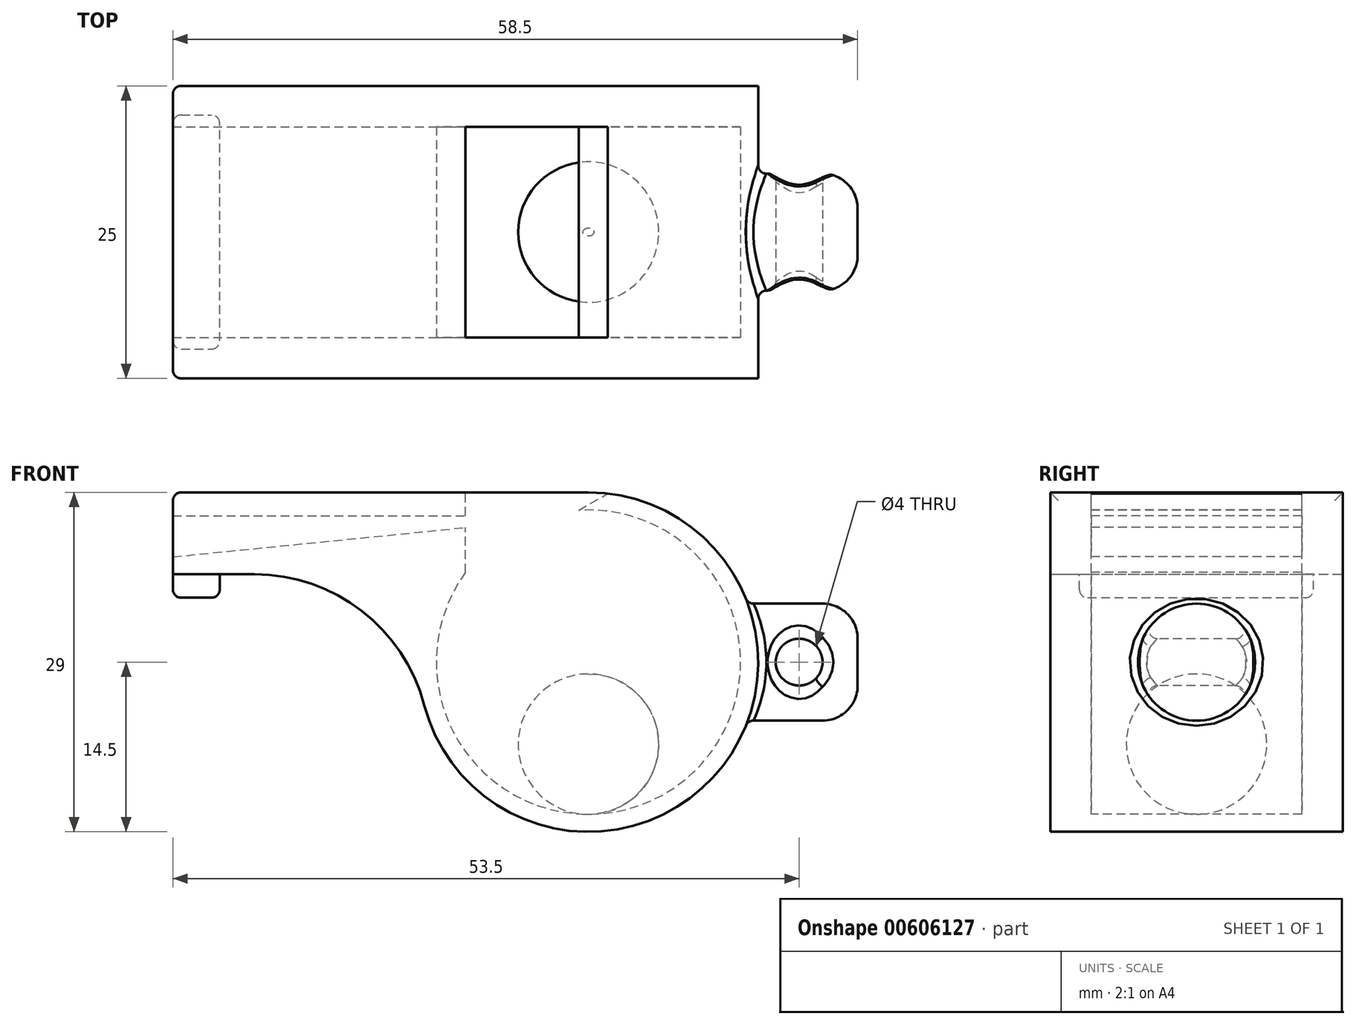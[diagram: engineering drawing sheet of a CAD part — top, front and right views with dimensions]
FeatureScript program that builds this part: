
annotation { "Feature Type Name" : "Feature", "Feature Type Description" : "" }
export const myFeature = defineFeature(function(context is Context, id is Id, definition is map)
    precondition{}
    {
        {
            var Q0;
            Q0=qCreatedBy(makeId("Front.planeOp"),FACE);
            var sketch = newSketch(context, id + "F0", { "sketchPlane" : qUnion([Q0])});
            skArc(sketch, "E0", {"start": v(-12.4, 7.5) * mm, "mid": v(7.12, -12.63) * mm, "end": v(0, 14.5) * mm});
            skLineSegment(sketch, "E1.bottom", {"start": v(0, 14.5) * mm, "end": v(-35.5, 14.5) * mm});
            skLineSegment(sketch, "E1.top", {"start": v(-12.4, 7.5) * mm, "end": v(-35.5, 7.5) * mm});
            skLineSegment(sketch, "E1.right", {"start": v(-35.5, 14.5) * mm, "end": v(-35.5, 7.5) * mm});
            skSolve(sketch);
        }
        {
            var Q0;
            Q0 = qSketchRegion(id + "F0", true);
            extrude(context, id + "F1", {"entities" : qUnion([Q0]), "endBound" : BoundingType.SYMMETRIC, "depth" : 25 * mm, "offsetDistance" : 25 * mm});
        }
        {
            var Q0;
            Q0=qCreatedBy(makeId("Front.planeOp"),FACE);
            var sketch = newSketch(context, id + "F2", { "sketchPlane" : qUnion([Q0])});
            skArc(sketch, "E2", {"start": v(-10.5, 7.66) * mm, "mid": v(5.89, -11.59) * mm, "end": v(0, 13) * mm});
            skLineSegment(sketch, "E3", {"start": v(-10.5, 7.66) * mm, "end": v(-10.5, 11.5) * mm});
            skLineSegment(sketch, "E4", {"start": v(-35.5, 12.5) * mm, "end": v(-10.5, 12.5) * mm});
            skLineSegment(sketch, "E5", {"start": v(-10.5, 12.5) * mm, "end": v(-10.5, 14.5) * mm});
            skLineSegment(sketch, "E6", {"start": v(-10.5, 14.5) * mm, "end": v(0, 14.5) * mm});
            skArc(sketch, "E7", {"start": v(-10.5, 7.66) * mm, "mid": v(6.26, -11.4) * mm, "end": v(-0.83, 12.97) * mm});
            skLineSegment(sketch, "E8", {"start": v(-35.5, 12.5) * mm, "end": v(-35.5, 9) * mm});
            skLineSegment(sketch, "E9", {"start": v(-35.5, 9) * mm, "end": v(-10.5, 11.5) * mm});
            skLineSegment(sketch, "E10", {"start": v(0, 13) * mm, "end": v(-0.83, 12.97) * mm});
            skLineSegment(sketch, "E11", {"start": v(0, 14.5) * mm, "end": v(1.81, 14.5) * mm});
            skLineSegment(sketch, "E12", {"start": v(-0.83, 12.97) * mm, "end": v(1.81, 14.5) * mm});
            skSolve(sketch);
        }
        {
            var Q0;
            Q0 = qSketchRegion(id + "F2", true);
            extrude(context, id + "F3", {"entities" : qUnion([Q0]), "operationType" : NewBodyOperationType.REMOVE, "endBound" : BoundingType.SYMMETRIC, "oppositeDirection" : true, "depth" : 18 * mm, "offsetDistance" : 25 * mm});
        }
        {
            var Q0;
            Q0=qCreatedBy(makeId("Front.planeOp"),FACE);
            var sketch = newSketch(context, id + "F4", { "sketchPlane" : qUnion([Q0])});
            skLineSegment(sketch, "E13", {"start": v(0, 0) * mm, "end": v(23, 0) * mm});
            skLineSegment(sketch, "E14.bottom", {"start": v(23, 0) * mm, "end": v(13, 0) * mm});
            skLineSegment(sketch, "E14.top", {"start": v(23, 5) * mm, "end": v(13, 5) * mm});
            skLineSegment(sketch, "E14.left", {"start": v(23, 0) * mm, "end": v(23, 5) * mm});
            skLineSegment(sketch, "E14.right", {"start": v(13, 0) * mm, "end": v(13, 5) * mm});
            skSolve(sketch);
        }
        {
            var Q0;
            Q0 = qSketchRegion(id + "F4", true);
            var Q1;
            Q1=sQuery(id+"F4.wireOp",EDGE,"E14.bottom");
            revolve(context, id + "F5", {"operationType" : NewBodyOperationType.ADD, "entities" : qUnion([Q0]), "axis" : qUnion([Q1]), "revolveType" : RevolveType.FULL});
        }
        {
            var Q0;
            Q0=makeQuery(id+"F5.opRevolve","SWEPT_EDGE",EDGE,{"disambiguationData":[OSD([sQuery(id+"F4.wireOp",EDGE,"E14.top"),sQuery(id+"F4.wireOp",EDGE,"E14.left")])]});
            fillet(context, id + "F6", {"entities" : qUnion([Q0]), "radius" : 3 * mm, "tangentPropagation" : true, "allowEdgeOverflow" : false});
        }
        {
            var Q0;
            Q0=qCreatedBy(makeId("Front.planeOp"),FACE);
            var sketch = newSketch(context, id + "F7", { "sketchPlane" : qUnion([Q0])});
            skCircle(sketch, "E15", {"center": v(18, 0) * mm, "radius": 2 * mm});
            skSolve(sketch);
        }
        {
            var Q0;
            Q0 = qSketchRegion(id + "F7", true);
            extrude(context, id + "F8", {"entities" : qUnion([Q0]), "operationType" : NewBodyOperationType.REMOVE, "endBound" : BoundingType.SYMMETRIC, "oppositeDirection" : true, "depth" : 10 * mm, "offsetDistance" : 25 * mm});
        }
        {
            var Q0;
            Q0=makeQuery(id+"F1.opExtrude","SWEPT_FACE",FACE,{"disambiguationData":[OSD([sQuery(id+"F0.wireOp",EDGE,"E1.top")])]});
            var sketch = newSketch(context, id + "F9", { "sketchPlane" : qUnion([Q0])});
            skLineSegment(sketch, "E16.bottom", {"start": v(-35.5, 10) * mm, "end": v(-31.5, 10) * mm});
            skLineSegment(sketch, "E16.top", {"start": v(-35.5, -10) * mm, "end": v(-31.5, -10) * mm});
            skLineSegment(sketch, "E16.left", {"start": v(-35.5, 10) * mm, "end": v(-35.5, -10) * mm});
            skLineSegment(sketch, "E16.right", {"start": v(-31.5, 10) * mm, "end": v(-31.5, -10) * mm});
            skSolve(sketch);
        }
        {
            var Q0;
            Q0 = qSketchRegion(id + "F9", true);
            extrude(context, id + "F10", {"entities" : qUnion([Q0]), "operationType" : NewBodyOperationType.ADD, "depth" : 2 * mm, "offsetDistance" : 25 * mm});
        }
        {
            var Q0;
            Q0=makeQuery(id+"F10.opExtrude","SWEPT_EDGE",EDGE,{"disambiguationData":[OSD([sQuery(id+"F0.wireOp",EDGE,"E1.top"),sQuery(id+"F0.wireOp",EDGE,"E1.right"),sQuery(id+"F9.wireOp",EDGE,"E16.bottom"),sQuery(id+"F9.wireOp",EDGE,"E16.left")])]});
            var Q1;
            Q1=makeQuery(id+"F10.opExtrude","CAP_EDGE",EDGE,{"disambiguationData":[OSD([sQuery(id+"F9.wireOp",EDGE,"E16.bottom")])],"isStart":false});
            var Q2;
            Q2=makeQuery(id+"F10.opExtrude","SWEPT_EDGE",EDGE,{"disambiguationData":[OSD([sQuery(id+"F9.wireOp",EDGE,"E16.bottom"),sQuery(id+"F9.wireOp",EDGE,"E16.right")])]});
            var Q3;
            Q3=makeQuery(id+"F10.opExtrude","CAP_EDGE",EDGE,{"disambiguationData":[OSD([sQuery(id+"F9.wireOp",EDGE,"E16.right")])],"isStart":false});
            var Q4;
            Q4=makeQuery(id+"F10.opExtrude","CAP_EDGE",EDGE,{"disambiguationData":[OSD([sQuery(id+"F9.wireOp",EDGE,"E16.top")])],"isStart":false});
            var Q5;
            Q5=makeQuery(id+"F10.opExtrude","CAP_EDGE",EDGE,{"disambiguationData":[OSD([sQuery(id+"F9.wireOp",EDGE,"E16.left")])],"isStart":false});
            var Q6;
            Q6=makeQuery(id+"F10.opExtrude","SWEPT_EDGE",EDGE,{"disambiguationData":[OSD([sQuery(id+"F9.wireOp",EDGE,"E16.top"),sQuery(id+"F9.wireOp",EDGE,"E16.right")])]});
            var Q7;
            Q7=makeQuery(id+"F10.opExtrude","SWEPT_EDGE",EDGE,{"disambiguationData":[OSD([sQuery(id+"F0.wireOp",EDGE,"E1.top"),sQuery(id+"F0.wireOp",EDGE,"E1.right"),sQuery(id+"F9.wireOp",EDGE,"E16.top"),sQuery(id+"F9.wireOp",EDGE,"E16.left")])]});
            var Q8;
            Q8=makeQuery(id+"F1.opExtrude","CAP_EDGE",EDGE,{"disambiguationData":[OSD([sQuery(id+"F0.wireOp",EDGE,"E1.right")])],"isStart":false});
            var Q9;
            Q9=makeQuery(id+"F1.opExtrude","SWEPT_EDGE",EDGE,{"disambiguationData":[OSD([sQuery(id+"F0.wireOp",EDGE,"E1.bottom"),sQuery(id+"F0.wireOp",EDGE,"E1.right")])]});
            var Q10;
            Q10=makeQuery(id+"F1.opExtrude","CAP_EDGE",EDGE,{"disambiguationData":[OSD([sQuery(id+"F0.wireOp",EDGE,"E1.right")])],"isStart":true});
            var Q11;
            {var subQ0=sQuery(id+"F4.wireOp",EDGE,"E14.left");Q11=makeQuery(id+"F6.opFillet","BLEND_EDGE",EDGE,{"blendedFrom":[makeQuery(id+"F5.opRevolve","SWEPT_EDGE",EDGE,{"disambiguationData":[OSD([sQuery(id+"F4.wireOp",EDGE,"E14.top"),subQ0])]}),makeQuery(id+"F5.opRevolve","SWEPT_FACE",FACE,{"disambiguationData":[OSD([subQ0])]})],"blendedInto":[makeQuery(id+"F5.opRevolve","SWEPT_FACE",FACE,{"disambiguationData":[OSD([subQ0])]})]});}
            var Q12;
            Q12=makeQuery(id+"F6.opFillet","BLEND_FACE",FACE,{"disambiguationData":[OSD([sQuery(id+"F4.wireOp",EDGE,"E14.top"),sQuery(id+"F4.wireOp",EDGE,"E14.left")])]});
            var Q13;
            Q13=makeQuery(id+"F5.boolean.opBoolean","INTERSECT",EDGE,{"derivedFrom":[makeQuery(id+"F1.opExtrude","SWEPT_FACE",FACE,{"disambiguationData":[OSD([sQuery(id+"F0.wireOp",EDGE,"E0")])]}),makeQuery(id+"F5.opRevolve","SWEPT_FACE",FACE,{"disambiguationData":[OSD([sQuery(id+"F4.wireOp",EDGE,"E14.top")])]})]});
            var Q14;
            Q14=makeQuery(id+"F5.opRevolve","SWEPT_FACE",FACE,{"disambiguationData":[OSD([sQuery(id+"F4.wireOp",EDGE,"E14.left")])]});
            var Q15;
            Q15=makeQuery(id+"F8.boolean.opBoolean","INTERSECT",EDGE,{"disambiguationData":[OD(0.0)],"derivedFrom":[makeQuery(id+"F5.opRevolve","SWEPT_FACE",FACE,{"disambiguationData":[OSD([sQuery(id+"F4.wireOp",EDGE,"E14.top")])]}),makeQuery(id+"F8.opExtrude","SWEPT_FACE",FACE,{"disambiguationData":[OSD([sQuery(id+"F7.wireOp",EDGE,"E15")])]})]});
            var Q16;
            Q16=makeQuery(id+"F8.boolean.opBoolean","INTERSECT",EDGE,{"disambiguationData":[OD(1.0)],"derivedFrom":[makeQuery(id+"F5.opRevolve","SWEPT_FACE",FACE,{"disambiguationData":[OSD([sQuery(id+"F4.wireOp",EDGE,"E14.top")])]}),makeQuery(id+"F8.opExtrude","SWEPT_FACE",FACE,{"disambiguationData":[OSD([sQuery(id+"F7.wireOp",EDGE,"E15")])]})]});
            var Q17;
            Q17=makeQuery(id+"F5.opRevolve","SWEPT_FACE",FACE,{"disambiguationData":[OSD([sQuery(id+"F4.wireOp",EDGE,"E14.top")])]});
            var Q18;
            {var subQ0=sQuery(id+"F4.wireOp",EDGE,"E14.top");Q18=makeQuery(id+"F8.boolean.opBoolean","SPLIT",EDGE,{"disambiguationData":[OD(0.0)],"derivedFrom":makeQuery(id+"F6.opFillet","BLEND_EDGE",EDGE,{"blendedFrom":[makeQuery(id+"F5.opRevolve","SWEPT_EDGE",EDGE,{"disambiguationData":[OSD([subQ0,sQuery(id+"F4.wireOp",EDGE,"E14.left")])]}),makeQuery(id+"F5.opRevolve","SWEPT_FACE",FACE,{"disambiguationData":[OSD([subQ0])]})],"blendedInto":[makeQuery(id+"F5.opRevolve","SWEPT_FACE",FACE,{"disambiguationData":[OSD([subQ0])]})]})});}
            var Q19;
            {var subQ0=sQuery(id+"F4.wireOp",EDGE,"E14.top");Q19=makeQuery(id+"F8.boolean.opBoolean","SPLIT",EDGE,{"disambiguationData":[OD(1.0)],"derivedFrom":makeQuery(id+"F6.opFillet","BLEND_EDGE",EDGE,{"blendedFrom":[makeQuery(id+"F5.opRevolve","SWEPT_EDGE",EDGE,{"disambiguationData":[OSD([subQ0,sQuery(id+"F4.wireOp",EDGE,"E14.left")])]}),makeQuery(id+"F5.opRevolve","SWEPT_FACE",FACE,{"disambiguationData":[OSD([subQ0])]})],"blendedInto":[makeQuery(id+"F5.opRevolve","SWEPT_FACE",FACE,{"disambiguationData":[OSD([subQ0])]})]})});}
            var Q20;
            Q20=makeQuery(id+"F8.boolean.opBoolean","COPY",FACE,{"derivedFrom":makeQuery(id+"F8.opExtrude","SWEPT_FACE",FACE,{"disambiguationData":[OSD([sQuery(id+"F7.wireOp",EDGE,"E15")])]})});
            fillet(context, id + "F11", {"entities" : qUnion([Q0, Q1, Q2, Q3, Q4, Q5, Q6, Q7, Q8, Q9, Q10, Q11, Q12, Q13, Q14, Q15, Q16, Q17, Q18, Q19, Q20]), "radius" : 0.7 * mm, "tangentPropagation" : true, "allowEdgeOverflow" : false});
        }
        {
            var Q0;
            Q0=makeQuery(id+"F1.opExtrude","SWEPT_EDGE",EDGE,{"disambiguationData":[OSD([sQuery(id+"F0.wireOp",EDGE,"E0"),sQuery(id+"F0.wireOp",EDGE,"E1.top")])]});
            fillet(context, id + "F12", {"entities" : qUnion([Q0]), "radius" : 15 * mm, "tangentPropagation" : true, "allowEdgeOverflow" : false});
        }
        {
            var Q0;
            Q0=qCreatedBy(makeId("Front.planeOp"),FACE);
            var sketch = newSketch(context, id + "F13", { "sketchPlane" : qUnion([Q0])});
            skArc(sketch, "E17", {"start": v(0, -13.01) * mm, "mid": v(6, -7.01) * mm, "end": v(0, -1.01) * mm});
            skLineSegment(sketch, "E18", {"start": v(0, -1.01) * mm, "end": v(0, -13.01) * mm});
            skLineSegment(sketch, "E19", {"start": v(0, -13.01) * mm, "end": v(0, -1.01) * mm});
            skLineSegment(sketch, "E20", {"start": v(0, -13.01) * mm, "end": v(17, -13.01) * mm});
            skSolve(sketch);
        }
        {
            var Q0;
            Q0 = qSketchRegion(id + "F13", true);
            var Q1;
            Q1=sQuery(id+"F13.wireOp",EDGE,"E19");
            revolve(context, id + "F14", {"operationType" : NewBodyOperationType.ADD, "entities" : qUnion([Q0]), "axis" : qUnion([Q1]), "revolveType" : RevolveType.FULL});
        }
    });
